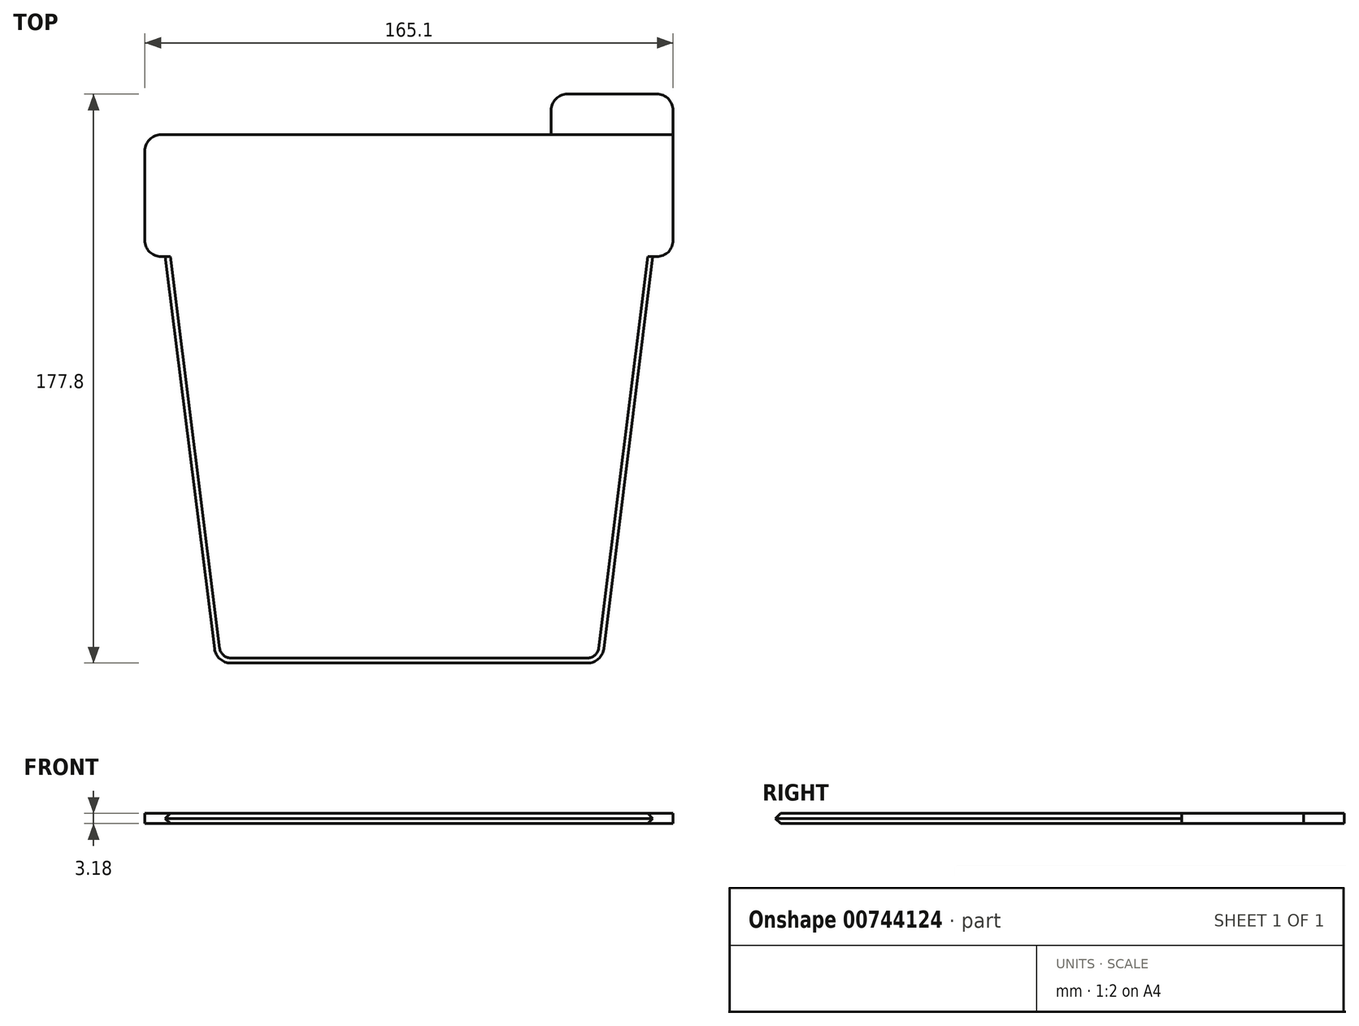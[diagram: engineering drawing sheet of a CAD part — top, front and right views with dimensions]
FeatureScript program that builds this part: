
annotation { "Feature Type Name" : "Feature", "Feature Type Description" : "" }
export const myFeature = defineFeature(function(context is Context, id is Id, definition is map)
    precondition{}
    {
        {
            var Q0;
            Q0=qCreatedBy(makeId("Top.planeOp"),FACE);
            var sketch = newSketch(context, id + "F0", { "sketchPlane" : qUnion([Q0])});
            skLineSegment(sketch, "E0.bottom", {"start": v(-82.55, 82.55) * mm, "end": v(82.55, 82.55) * mm});
            skLineSegment(sketch, "E0.top", {"start": v(-82.55, -82.55) * mm, "end": v(82.55, -82.55) * mm});
            skLineSegment(sketch, "E0.left", {"start": v(-82.55, 82.55) * mm, "end": v(-82.55, -82.55) * mm});
            skLineSegment(sketch, "E0.right", {"start": v(82.55, 82.55) * mm, "end": v(82.55, -82.55) * mm});
            skPoint(sketch, "E0.middle", {"position": v(0, 0) * mm});
            skSolve(sketch);
        }
        {
            var Q0;
            Q0=makeQuery(id+"F0.imprint","IMPRINT",FACE,{"disambiguationData":[TD([[makeQuery(id+"F0.imprint","IMPRINT",EDGE,{"derivedFrom":sQuery(id+"F0.wireOp",EDGE,"E0.bottom")}),-1.0]])]});
            var sketch = newSketch(context, id + "F1", { "sketchPlane" : qUnion([Q0])});
            skLineSegment(sketch, "E1", {"start": v(-82.55, 82.55) * mm, "end": v(-82.55, 44.45) * mm});
            skLineSegment(sketch, "E2", {"start": v(-82.55, 44.45) * mm, "end": v(-76.2, 44.45) * mm});
            skLineSegment(sketch, "E3", {"start": v(-76.2, 44.45) * mm, "end": v(-60.2, -82.55) * mm});
            skLineSegment(sketch, "E4", {"start": v(-60.2, -82.55) * mm, "end": v(60.33, -82.55) * mm});
            skLineSegment(sketch, "E5", {"start": v(60.33, -82.55) * mm, "end": v(76.2, 44.45) * mm});
            skLineSegment(sketch, "E6", {"start": v(76.2, 44.45) * mm, "end": v(82.55, 44.45) * mm});
            skLineSegment(sketch, "E7", {"start": v(82.55, 44.45) * mm, "end": v(82.55, 82.55) * mm});
            skLineSegment(sketch, "E8", {"start": v(82.55, 82.55) * mm, "end": v(-82.55, 82.55) * mm});
            skSolve(sketch);
        }
        {
            var Q0;
            Q0 = qSketchRegion(id + "F1", true);
            extrude(context, id + "F2", {"entities" : qUnion([Q0]), "depth" : 3.17 * mm, "offsetDistance" : 25.4 * mm});
        }
        {
            var Q0;
            Q0=makeQuery(id+"F0.imprint","IMPRINT",FACE,{"disambiguationData":[TD([[makeQuery(id+"F0.imprint","IMPRINT",EDGE,{"derivedFrom":sQuery(id+"F0.wireOp",EDGE,"E0.bottom")}),-1.0]])]});
            var sketch = newSketch(context, id + "F3", { "sketchPlane" : qUnion([Q0])});
            skLineSegment(sketch, "E9.bottom", {"start": v(82.55, 82.55) * mm, "end": v(44.45, 82.55) * mm});
            skLineSegment(sketch, "E9.top", {"start": v(82.55, 95.25) * mm, "end": v(44.45, 95.25) * mm});
            skLineSegment(sketch, "E9.left", {"start": v(82.55, 82.55) * mm, "end": v(82.55, 95.25) * mm});
            skLineSegment(sketch, "E9.right", {"start": v(44.45, 82.55) * mm, "end": v(44.45, 95.25) * mm});
            skSolve(sketch);
        }
        {
            var Q0;
            Q0 = qSketchRegion(id + "F3", true);
            extrude(context, id + "F4", {"entities" : qUnion([Q0]), "depth" : 3.17 * mm, "offsetDistance" : 25.4 * mm});
        }
        {
            var Q0;
            Q0=makeQuery(id+"F2.opExtrude","SWEPT_EDGE",EDGE,{"disambiguationData":[OSD([sQuery(id+"F0.wireOp",EDGE,"E0.left"),sQuery(id+"F1.wireOp",EDGE,"E1"),sQuery(id+"F1.wireOp",EDGE,"E2")])]});
            var Q1;
            Q1=makeQuery(id+"F2.opExtrude","SWEPT_EDGE",EDGE,{"disambiguationData":[OSD([sQuery(id+"F1.wireOp",EDGE,"E1"),sQuery(id+"F1.wireOp",EDGE,"E8")])]});
            var Q2;
            Q2=makeQuery(id+"F4.opExtrude","SWEPT_EDGE",EDGE,{"disambiguationData":[OSD([sQuery(id+"F3.wireOp",EDGE,"E9.top"),sQuery(id+"F3.wireOp",EDGE,"E9.right")])]});
            var Q3;
            Q3=makeQuery(id+"F4.opExtrude","SWEPT_EDGE",EDGE,{"disambiguationData":[OSD([sQuery(id+"F3.wireOp",EDGE,"E9.top"),sQuery(id+"F3.wireOp",EDGE,"E9.left")])]});
            var Q4;
            Q4=makeQuery(id+"F2.opExtrude","SWEPT_EDGE",EDGE,{"disambiguationData":[OSD([sQuery(id+"F0.wireOp",EDGE,"E0.right"),sQuery(id+"F1.wireOp",EDGE,"E6"),sQuery(id+"F1.wireOp",EDGE,"E7")])]});
            var Q5;
            Q5=makeQuery(id+"F2.opExtrude","SWEPT_EDGE",EDGE,{"disambiguationData":[OSD([sQuery(id+"F0.wireOp",EDGE,"E0.top"),sQuery(id+"F1.wireOp",EDGE,"E4"),sQuery(id+"F1.wireOp",EDGE,"E5")])]});
            var Q6;
            Q6=makeQuery(id+"F2.opExtrude","SWEPT_EDGE",EDGE,{"disambiguationData":[OSD([sQuery(id+"F0.wireOp",EDGE,"E0.top"),sQuery(id+"F1.wireOp",EDGE,"E3"),sQuery(id+"F1.wireOp",EDGE,"E4")])]});
            fillet(context, id + "F5", {"entities" : qUnion([Q0, Q1, Q2, Q3, Q4, Q5, Q6]), "radius" : 5.08 * mm, "tangentPropagation" : true, "allowEdgeOverflow" : false});
        }
        {
            var Q0;
            Q0=makeQuery(id+"F2.opExtrude","SWEPT_FACE",FACE,{"disambiguationData":[OSD([sQuery(id+"F1.wireOp",EDGE,"E4")])]});
            var Q1;
            Q1=makeQuery(id+"F5.opFillet","BLEND_FACE",FACE,{"disambiguationData":[OSD([sQuery(id+"F0.wireOp",EDGE,"E0.top"),sQuery(id+"F1.wireOp",EDGE,"E3"),sQuery(id+"F1.wireOp",EDGE,"E4")])]});
            var Q2;
            Q2=makeQuery(id+"F5.opFillet","BLEND_FACE",FACE,{"disambiguationData":[OSD([sQuery(id+"F0.wireOp",EDGE,"E0.top"),sQuery(id+"F1.wireOp",EDGE,"E4"),sQuery(id+"F1.wireOp",EDGE,"E5")])]});
            chamfer(context, id + "F6", {"entities" : qUnion([Q0, Q1, Q2]), "width" : 1.59 * mm, "tangentPropagation" : true});
        }
    });
